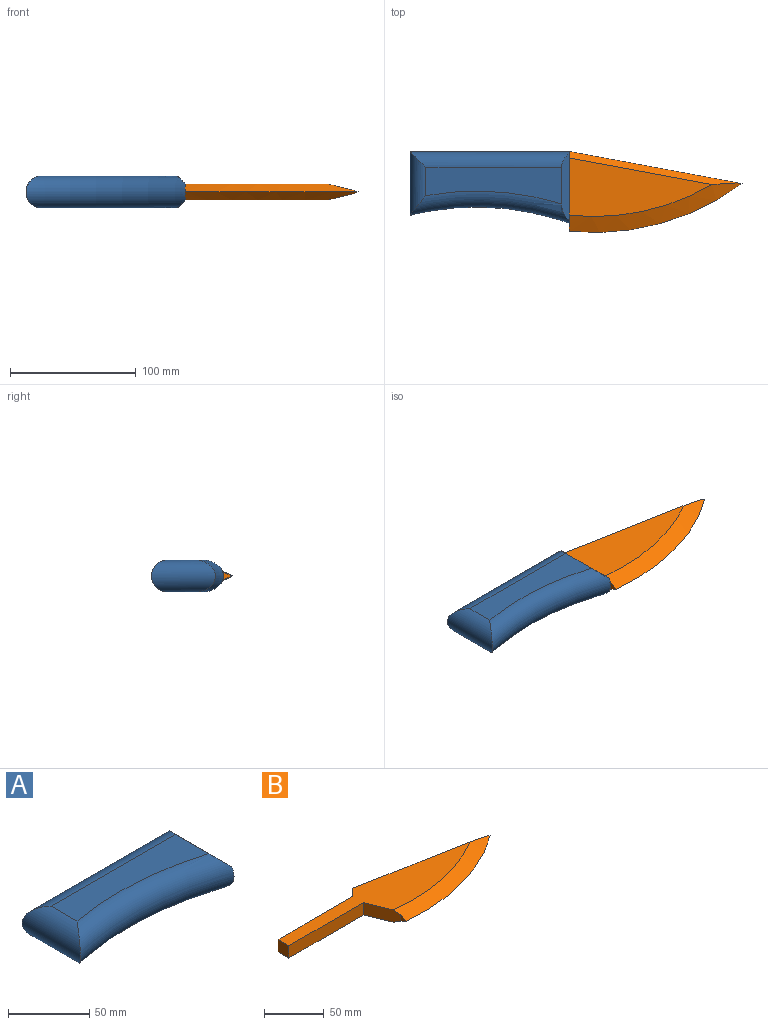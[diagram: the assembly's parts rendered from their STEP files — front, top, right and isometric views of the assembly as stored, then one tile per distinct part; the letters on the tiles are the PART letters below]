
ASSEMBLY  parts=2 mates=1
PART A: 16 faces, bbox 151.3x57.3x25.5 mm
  f0: plane 56.39x3.25mm, normal (1,0,0), area 175.1mm2, adj f7,f12,f13,f15
  f1: plane 56.39x3.25mm, normal (1,0,0), area 175.1mm2, adj f5,f11,f13,f15
  f2: plane 107.95x28.94mm, normal (0,0,1), area 2304mm2, adj f11,f13,f14,f15
  f3: plane 107.95x28.94mm, normal (0,0,-1), area 2304mm2, adj f12,f13,f14,f15
  f4: plane 88.9x6.35mm, normal (0,-1,0), area 564.5mm2, adj f5,f7,f8,f9
  f5: plane 101.6x56.32mm, normal (0,0,-1), area 1572.5mm2, adj f1,f4,f6,f8,f9,f10,f13,f15
  f6: plane 88.9x6.35mm, normal (0,1,0), area 564.5mm2, adj f5,f7,f8,f10
  f7: plane 101.6x56.32mm, normal (0,0,1), area 1572.5mm2, adj f0,f4,f6,f8,f9,f10,f13,f15
  f8: plane 12.7x6.35mm, normal (1,0,0), area 80.6mm2, adj f4,f5,f6,f7
  f9: plane 12.7x12.7mm, normal (0.71,-0.71,0), area 112.8mm2, adj f4,f5,f7,f13
  f10: plane 31.75x12.7mm, normal (0.93,0.37,0), area 216mm2, adj f5,f6,f7,f15
  f11: plane 53.64x6.35mm, normal (0.71,0,0.71), area 412.8mm2, adj f1,f2,f13,f15
  f12: plane 53.64x6.35mm, normal (0.71,0,-0.71), area 412.8mm2, adj f0,f3,f13,f15
  f13: cylinder r=12.7mm len=127.04mm, axis (1,0,0), area 4771.6mm2, adj f0,f1,f2,f3,f5,f7,f9,f11
  f14: cylinder r=12.7mm len=50.84mm, axis (0,1,0), area 1611.8mm2, adj f2,f3,f13,f15
  f15: torus R=229.91mm, axis (0,0,1), area 4839.6mm2, adj f0,f1,f2,f3,f5,f7,f10,f11
PART B: 13 faces, bbox 239x64.5x12.7 mm
  f0: plane 88.9x12.7mm, normal (0,-1,0), area 1129mm2, adj f3,f6,f7,f8
  f1: plane 12.7x12.7mm, normal (-0.71,0.71,0), area 196.8mm2, adj f2,f5,f6,f7,f11,f12
  f2: plane 88.9x12.7mm, normal (0,1,0), area 1129mm2, adj f1,f3,f6,f7
  f3: plane 12.7x12.7mm, normal (-1,0,0), area 161.3mm2, adj f0,f2,f6,f7
  f4: plane 6.36x6.33mm, normal (-1,0,0), area 20.1mm2, adj f8,f9,f10
  f5: plane 137.39x25.59mm, normal (0.18,0.98,0), area 350.5mm2, adj f1,f9,f10,f11,f12
  f6: plane 214.94x47.42mm, normal (0,0,1), area 4858.6mm2, adj f0,f1,f2,f3,f8,f9,f12
  f7: plane 214.94x47.42mm, normal (0,0,-1), area 4858.6mm2, adj f0,f1,f2,f3,f8,f10,f11
  f8: plane 31.75x12.7mm, normal (-0.93,-0.37,0), area 411.2mm2, adj f0,f4,f6,f7,f9,f10
  f9: cone r=185.1mm half-angle=63.4deg, axis (0,0,-1), area 1894.9mm2, adj f4,f5,f6,f8,f10,f12
  f10: cone r=197.8mm half-angle=63.4deg, axis (0,0,1), area 1894.9mm2, adj f4,f5,f7,f8,f9,f11
  f11: plane 138.3x26.27mm, normal (0.13,0.7,-0.71), area 920.9mm2, adj f1,f5,f7,f10
  f12: plane 138.3x26.27mm, normal (0.13,0.7,0.71), area 920.9mm2, adj f1,f5,f6,f9
PLACE A t=(75.22,52.2,-10.65)mm
PLACE B t=(90.8,64.22,2.05)mm
MATE fastened A.f8 <-> B.f3  axis (1,0,0) through (-10.8,70.57,2.05)mm
